# Revit family: Холодильные столы среднетемпературные
name_source: partatom
category: Оборудование
units: mm (PartAtom-declared; Revit-internal decimal feet)

## family parameters
Всегда вертикально = Да
Классификация = Нет
На основе рабочей плоскости = Нет
Общий = Нет
При загрузке вырезать с полостями = Нет
Размер круглого соединителя = Использовать диаметр
Тип детали = Нормальный
Точка расчета площади = Нет

## types (32) — shared parameters
Высота = 850 мм
Диап. рабочих темп. = -2....+10
Напряжение питания = 230.00 В
Степень защиты = IP24
Таблица поиска = ТМ
Температура окр. среды = +12.....-43
Терморегулятор = эл. блок
Тип оттайки = авт. с системой исп. конденсата
Тип охлаждения = динамический
Условия окр. среды (темп/влажн) = до +43/до 80
Хладаген = R134a
Холодильный стол = нержавеющая сталь
zero-valued in all types: Отметка по умолчанию

## per-type parameters (varying)
- ТМ2-GC: Боковая панель упр.=Да; Вес нетто/брутто, кг=125/140; Габаритные размеры, мм=1200х604х850/910; Глубина=604 мм; Двери 012-GC=Нет; Дверь G - 1=Нет; Дверь G-2=Нет; Дверь G-3=Нет; Дверь G-4=Нет; Дверь GC=Да; Количество дверей=2; Нижнее распол Дверь -1=Нет; Нижнее распол. Дверь -2=Нет; Нижняя панель упр.=Нет; Объем, л=270; Размеры в упоковке, мм=1310х715х1045; Столешница закругл.=Нет; Столешница квадр.=Да; Цена, руб=53 646; Число дверей=2; Ширина=1200 мм; Шкаф выдв. двойной - 1=Нет; Шкаф выдв. тройной - 1=Нет; Шкаф выдв. тройной - 2=Нет; Шкаф выдв.двойной - 2=Нет
- ТМ3-GC: Боковая панель упр.=Да; Вес нетто/брутто, кг=145/170; Габаритные размеры, мм=1630х605х850/910; Глубина=605 мм; Двери 012-GC=Нет; Дверь G - 1=Нет; Дверь G-2=Нет; Дверь G-3=Нет; Дверь G-4=Нет; Дверь GC=Да; Количество дверей=3; Нижнее распол Дверь -1=Нет; Нижнее распол. Дверь -2=Нет; Нижняя панель упр.=Нет; Объем, л=400; Размеры в упоковке, мм=1725х715х1045; Столешница закругл.=Нет; Столешница квадр.=Да; Цена, руб=63 011; Число дверей=3; Ширина=1630 мм; Шкаф выдв. двойной - 1=Нет; Шкаф выдв. тройной - 1=Нет; Шкаф выдв. тройной - 2=Нет; Шкаф выдв.двойной - 2=Нет
- TM4-GC: Боковая панель упр.=Да; Вес нетто/брутто, кг=165/190; Габаритные размеры, мм=2060х605х850/910; Глубина=605 мм; Двери 012-GC=Нет; Дверь G - 1=Нет; Дверь G-2=Нет; Дверь G-3=Нет; Дверь G-4=Нет; Дверь GC=Да; Количество дверей=4; Нижнее распол Дверь -1=Нет; Нижнее распол. Дверь -2=Нет; Нижняя панель упр.=Нет; Объем, л=500; Размеры в упоковке, мм=2165х715х1045; Столешница закругл.=Нет; Столешница квадр.=Да; Цена, руб=77 746; Число дверей=4; Ширина=2060 мм; Шкаф выдв. двойной - 1=Нет; Шкаф выдв. тройной - 1=Нет; Шкаф выдв. тройной - 2=Нет; Шкаф выдв.двойной - 2=Нет
- TM2GN-GC: Боковая панель упр.=Да; Вес нетто/брутто, кг=130/150; Габаритные размеры, мм=1200х605х850/910; Глубина=705 мм; Двери 012-GC=Нет; Дверь G - 1=Нет; Дверь G-2=Нет; Дверь G-3=Нет; Дверь G-4=Нет; Дверь GC=Да; Количество дверей=2; Нижнее распол Дверь -1=Нет; Нижнее распол. Дверь -2=Нет; Нижняя панель упр.=Нет; Объем, л=320; Размеры в упоковке, мм=1310х815х1045; Столешница закругл.=Нет; Столешница квадр.=Да; Цена, руб=55 169; Число дверей=2; Ширина=1200 мм; Шкаф выдв. двойной - 1=Нет; Шкаф выдв. тройной - 1=Нет; Шкаф выдв. тройной - 2=Нет; Шкаф выдв.двойной - 2=Нет
- TM3GN-GC: Боковая панель упр.=Да; Вес нетто/брутто, кг=150/180; Габаритные размеры, мм=1630х605х850/910; Глубина=705 мм; Двери 012-GC=Нет; Дверь G - 1=Нет; Дверь G-2=Нет; Дверь G-3=Нет; Дверь G-4=Нет; Дверь GC=Да; Количество дверей=3; Нижнее распол Дверь -1=Нет; Нижнее распол. Дверь -2=Нет; Нижняя панель упр.=Нет; Объем, л=450; Размеры в упоковке, мм=1725х815х1045; Столешница закругл.=Нет; Столешница квадр.=Да; Цена, руб=64 254; Число дверей=3; Ширина=1630 мм; Шкаф выдв. двойной - 1=Нет; Шкаф выдв. тройной - 1=Нет; Шкаф выдв. тройной - 2=Нет; Шкаф выдв.двойной - 2=Нет
- TM4GN-GC: Боковая панель упр.=Да; Вес нетто/брутто, кг=165/200; Габаритные размеры, мм=2060х605х850/910; Глубина=705 мм; Двери 012-GC=Нет; Дверь G - 1=Нет; Дверь G-2=Нет; Дверь G-3=Нет; Дверь G-4=Нет; Дверь GC=Да; Количество дверей=4; Нижнее распол Дверь -1=Нет; Нижнее распол. Дверь -2=Нет; Нижняя панель упр.=Нет; Объем, л=600; Размеры в упоковке, мм=2165х815х1045; Столешница закругл.=Нет; Столешница квадр.=Да; Цена, руб=78 641; Число дверей=4; Ширина=2060 мм; Шкаф выдв. двойной - 1=Нет; Шкаф выдв. тройной - 1=Нет; Шкаф выдв. тройной - 2=Нет; Шкаф выдв.двойной - 2=Нет
- TM2-G: Боковая панель упр.=Да; Вес нетто/брутто, кг=125/140; Габаритные размеры, мм=1200х604х850/910; Глубина=604 мм; Двери 012-GC=Нет; Дверь G - 1=Да; Дверь G-2=Да; Дверь G-3=Нет; Дверь G-4=Нет; Дверь GC=Нет; Количество дверей=2; Нижнее распол Дверь -1=Нет; Нижнее распол. Дверь -2=Нет; Нижняя панель упр.=Нет; Объем, л=270; Размеры в упоковке, мм=1310х715х1045; Столешница закругл.=Да; Столешница квадр.=Нет; Цена, руб=55 418; Число дверей=2; Ширина=1200 мм; Шкаф выдв. двойной - 1=Нет; Шкаф выдв. тройной - 1=Нет; Шкаф выдв. тройной - 2=Нет; Шкаф выдв.двойной - 2=Нет
- TM-4G: Боковая панель упр.=Да; Вес нетто/брутто, кг=160/190; Габаритные размеры, мм=2060х605х850/910; Глубина=605 мм; Двери 012-GC=Нет; Дверь G - 1=Да; Дверь G-2=Да; Дверь G-3=Да; Дверь G-4=Да; Дверь GC=Нет; Количество дверей=4; Нижнее распол Дверь -1=Нет; Нижнее распол. Дверь -2=Нет; Нижняя панель упр.=Нет; Объем, л=500; Размеры в упоковке, мм=2165х715х1045; Столешница закругл.=Да; Столешница квадр.=Нет; Цена, руб=78 828; Число дверей=2; Ширина=2060 мм; Шкаф выдв. двойной - 1=Нет; Шкаф выдв. тройной - 1=Нет; Шкаф выдв. тройной - 2=Нет; Шкаф выдв.двойной - 2=Нет
- ТМ3-G: Боковая панель упр.=Да; Вес нетто/брутто, кг=145/170; Габаритные размеры, мм=1630х605х850/910; Глубина=605 мм; Двери 012-GC=Нет; Дверь G - 1=Да; Дверь G-2=Да; Дверь G-3=Нет; Дверь G-4=Да; Дверь GC=Нет; Количество дверей=3; Нижнее распол Дверь -1=Нет; Нижнее распол. Дверь -2=Нет; Нижняя панель упр.=Нет; Объем, л=400; Размеры в упоковке, мм=1725х715х1045; Столешница закругл.=Да; Столешница квадр.=Нет; Цена, руб=65 047; Число дверей=2; Ширина=1630 мм; Шкаф выдв. двойной - 1=Нет; Шкаф выдв. тройной - 1=Нет; Шкаф выдв. тройной - 2=Нет; Шкаф выдв.двойной - 2=Нет
- TM2-22-G: Боковая панель упр.=Да; Вес нетто/брутто, кг=135/150; Габаритные размеры, мм=1200х605х850/910; Глубина=605 мм; Двери 012-GC=Нет; Дверь G - 1=Нет; Дверь G-2=Нет; Дверь G-3=Нет; Дверь G-4=Нет; Дверь GC=Нет; Количество дверей=2; Нижнее распол Дверь -1=Нет; Нижнее распол. Дверь -2=Нет; Нижняя панель упр.=Нет; Объем, л=270; Размеры в упоковке, мм=1310х715х1045; Столешница закругл.=Да; Столешница квадр.=Нет; Цена, руб=88 198; Число дверей=2; Ширина=1200 мм; Шкаф выдв. двойной - 1=Да; Шкаф выдв. тройной - 1=Нет; Шкаф выдв. тройной - 2=Нет; Шкаф выдв.двойной - 2=Да
- TM3-222-G: Боковая панель упр.=Да; Вес нетто/брутто, кг=160/185; Габаритные размеры, мм=1630х605х850/910; Глубина=605 мм; Двери 012-GC=Нет; Дверь G - 1=Нет; Дверь G-2=Нет; Дверь G-3=Нет; Дверь G-4=Нет; Дверь GC=Нет; Количество дверей=6; Нижнее распол Дверь -1=Нет; Нижнее распол. Дверь -2=Нет; Нижняя панель упр.=Нет; Объем, л=400; Размеры в упоковке, мм=1725х715х1045; Столешница закругл.=Да; Столешница квадр.=Нет; Цена, руб=114 216; Число дверей=2; Ширина=1630 мм; Шкаф выдв. двойной - 1=Да; Шкаф выдв. тройной - 1=Нет; Шкаф выдв. тройной - 2=Нет; Шкаф выдв.двойной - 2=Да
- TM3GN-222-G: Боковая панель упр.=Да; Вес нетто/брутто, кг=165/195; Габаритные размеры, мм=1630х705х850/910; Глубина=705 мм; Двери 012-GC=Нет; Дверь G - 1=Нет; Дверь G-2=Нет; Дверь G-3=Нет; Дверь G-4=Нет; Дверь GC=Нет; Количество дверей=6; Нижнее распол Дверь -1=Нет; Нижнее распол. Дверь -2=Нет; Нижняя панель упр.=Нет; Объем, л=450; Размеры в упоковке, мм=1725х815х1045; Столешница закругл.=Да; Столешница квадр.=Нет; Цена, руб=116 511; Число дверей=2; Ширина=1630 мм; Шкаф выдв. двойной - 1=Да; Шкаф выдв. тройной - 1=Нет; Шкаф выдв. тройной - 2=Нет; Шкаф выдв.двойной - 2=Да
- TM2GN-22-G: Боковая панель упр.=Да; Вес нетто/брутто, кг=140/160; Габаритные размеры, мм=1200х705х850/910; Глубина=705 мм; Двери 012-GC=Нет; Дверь G - 1=Нет; Дверь G-2=Нет; Дверь G-3=Нет; Дверь G-4=Нет; Дверь GC=Нет; Количество дверей=4; Нижнее распол Дверь -1=Нет; Нижнее распол. Дверь -2=Нет; Нижняя панель упр.=Нет; Объем, л=320; Размеры в упоковке, мм=1310х815х1045; Столешница закругл.=Да; Столешница квадр.=Нет; Цена, руб=89 679; Число дверей=2; Ширина=1200 мм; Шкаф выдв. двойной - 1=Да; Шкаф выдв. тройной - 1=Нет; Шкаф выдв. тройной - 2=Нет; Шкаф выдв.двойной - 2=Да
- TM2-20-G: Боковая панель упр.=Да; Вес нетто/брутто, кг=130/145; Габаритные размеры, мм=1200х605х850/910; Глубина=605 мм; Двери 012-GC=Нет; Дверь G - 1=Нет; Дверь G-2=Да; Дверь G-3=Нет; Дверь G-4=Нет; Дверь GC=Нет; Количество дверей=2; Нижнее распол Дверь -1=Нет; Нижнее распол. Дверь -2=Нет; Нижняя панель упр.=Нет; Объем, л=270; Размеры в упоковке, мм=1310х715х1045; Столешница закругл.=Да; Столешница квадр.=Нет; Цена, руб=71 808; Число дверей=2; Ширина=1200 мм; Шкаф выдв. двойной - 1=Да; Шкаф выдв. тройной - 1=Нет; Шкаф выдв. тройной - 2=Нет; Шкаф выдв.двойной - 2=Нет
- TM2GN-20-G: Боковая панель упр.=Да; Вес нетто/брутто, кг=135/155; Габаритные размеры, мм=1200х705х850/910; Глубина=705 мм; Двери 012-GC=Нет; Дверь G - 1=Нет; Дверь G-2=Да; Дверь G-3=Нет; Дверь G-4=Нет; Дверь GC=Нет; Количество дверей=2; Нижнее распол Дверь -1=Нет; Нижнее распол. Дверь -2=Нет; Нижняя панель упр.=Нет; Объем, л=320; Размеры в упоковке, мм=1310х815х1045; Столешница закругл.=Да; Столешница квадр.=Нет; Цена, руб=73 289; Число дверей=2; Ширина=1200 мм; Шкаф выдв. двойной - 1=Да; Шкаф выдв. тройной - 1=Нет; Шкаф выдв. тройной - 2=Нет; Шкаф выдв.двойной - 2=Нет
- TM2-33-G: Боковая панель упр.=Да; Вес нетто/брутто, кг=135/150; Габаритные размеры, мм=1200х605х850/910; Глубина=605 мм; Двери 012-GC=Нет; Дверь G - 1=Нет; Дверь G-2=Нет; Дверь G-3=Нет; Дверь G-4=Нет; Дверь GC=Нет; Количество дверей=2; Нижнее распол Дверь -1=Нет; Нижнее распол. Дверь -2=Нет; Нижняя панель упр.=Нет; Объем, л=270; Размеры в упоковке, мм=1310х715х1045; Столешница закругл.=Да; Столешница квадр.=Нет; Цена, руб=93 198; Число дверей=2; Ширина=1200 мм; Шкаф выдв. двойной - 1=Нет; Шкаф выдв. тройной - 1=Да; Шкаф выдв. тройной - 2=Да; Шкаф выдв.двойной - 2=Нет
- TM3-333-G: Боковая панель упр.=Да; Вес нетто/брутто, кг=160/185; Габаритные размеры, мм=1630х605х850/910; Глубина=605 мм; Двери 012-GC=Нет; Дверь G - 1=Нет; Дверь G-2=Нет; Дверь G-3=Нет; Дверь G-4=Нет; Дверь GC=Нет; Количество дверей=9; Нижнее распол Дверь -1=Нет; Нижнее распол. Дверь -2=Нет; Нижняя панель упр.=Нет; Объем, л=400; Размеры в упоковке, мм=1725х715х1045; Столешница закругл.=Да; Столешница квадр.=Нет; Цена, руб=121 716; Число дверей=2; Ширина=1630 мм; Шкаф выдв. двойной - 1=Нет; Шкаф выдв. тройной - 1=Да; Шкаф выдв. тройной - 2=Да; Шкаф выдв.двойной - 2=Нет
- TM2-03-G: Боковая панель упр.=Да; Вес нетто/брутто, кг=135/150; Габаритные размеры, мм=1200х605х850/910; Глубина=605 мм; Двери 012-GC=Нет; Дверь G - 1=Нет; Дверь G-2=Да; Дверь G-3=Нет; Дверь G-4=Нет; Дверь GC=Нет; Количество дверей=2; Нижнее распол Дверь -1=Нет; Нижнее распол. Дверь -2=Нет; Нижняя панель упр.=Нет; Объем, л=270; Размеры в упоковке, мм=1310х715х1045; Столешница закругл.=Да; Столешница квадр.=Нет; Цена, руб=74 308; Число дверей=2; Ширина=1200 мм; Шкаф выдв. двойной - 1=Нет; Шкаф выдв. тройной - 1=Да; Шкаф выдв. тройной - 2=Нет; Шкаф выдв.двойной - 2=Нет
- TM2GN-03-G: Боковая панель упр.=Да; Вес нетто/брутто, кг=135/155; Габаритные размеры, мм=1200х705х850/910; Глубина=705 мм; Двери 012-GC=Нет; Дверь G - 1=Нет; Дверь G-2=Да; Дверь G-3=Нет; Дверь G-4=Нет; Дверь GC=Нет; Количество дверей=2; Нижнее распол Дверь -1=Нет; Нижнее распол. Дверь -2=Нет; Нижняя панель упр.=Нет; Объем, л=270; Размеры в упоковке, мм=1310х815х1045; Столешница закругл.=Да; Столешница квадр.=Нет; Цена, руб=75 789; Число дверей=2; Ширина=1200 мм; Шкаф выдв. двойной - 1=Нет; Шкаф выдв. тройной - 1=Да; Шкаф выдв. тройной - 2=Нет; Шкаф выдв.двойной - 2=Нет
- TM3GN-333-G: Боковая панель упр.=Да; Вес нетто/брутто, кг=165/195; Габаритные размеры, мм=1630х705х850/910; Глубина=705 мм; Двери 012-GC=Нет; Дверь G - 1=Нет; Дверь G-2=Нет; Дверь G-3=Нет; Дверь G-4=Нет; Дверь GC=Нет; Количество дверей=9; Нижнее распол Дверь -1=Нет; Нижнее распол. Дверь -2=Нет; Нижняя панель упр.=Нет; Объем, л=450; Размеры в упоковке, мм=1725х815х1045; Столешница закругл.=Да; Столешница квадр.=Нет; Цена, руб=124 011; Число дверей=2; Ширина=1630 мм; Шкаф выдв. двойной - 1=Нет; Шкаф выдв. тройной - 1=Да; Шкаф выдв. тройной - 2=Да; Шкаф выдв.двойной - 2=Нет
- TM2GN-33-G: Боковая панель упр.=Да; Вес нетто/брутто, кг=140/160; Габаритные размеры, мм=1200х705х850/910; Глубина=705 мм; Двери 012-GC=Нет; Дверь G - 1=Нет; Дверь G-2=Нет; Дверь G-3=Нет; Дверь G-4=Нет; Дверь GC=Нет; Количество дверей=2; Нижнее распол Дверь -1=Нет; Нижнее распол. Дверь -2=Нет; Нижняя панель упр.=Нет; Объем, л=320; Размеры в упоковке, мм=1310х815х1045; Столешница закругл.=Да; Столешница квадр.=Нет; Цена, руб=94 679; Число дверей=2; Ширина=1200 мм; Шкаф выдв. двойной - 1=Нет; Шкаф выдв. тройной - 1=Да; Шкаф выдв. тройной - 2=Да; Шкаф выдв.двойной - 2=Нет
- TM3GN-012-GC: Боковая панель упр.=Да; Вес нетто/брутто, кг=160/190; Габаритные размеры, мм=1630х705х850/910; Глубина=705 мм; Двери 012-GC=Да; Дверь G - 1=Нет; Дверь G-2=Нет; Дверь G-3=Нет; Дверь G-4=Нет; Дверь GC=Нет; Количество дверей=5; Нижнее распол Дверь -1=Нет; Нижнее распол. Дверь -2=Нет; Нижняя панель упр.=Нет; Объем, л=450; Размеры в упоковке, мм=1725х815х1045; Столешница закругл.=Нет; Столешница квадр.=Да; Число дверей=3; Ширина=1630 мм; Шкаф выдв. двойной - 1=Нет; Шкаф выдв. тройной - 1=Нет; Шкаф выдв. тройной - 2=Нет; Шкаф выдв.двойной - 2=Нет
- TM3-012-GC: Боковая панель упр.=Да; Вес нетто/брутто, кг=140/180; Габаритные размеры, мм=1630х605х850/910; Глубина=605 мм; Двери 012-GC=Да; Дверь G - 1=Нет; Дверь G-2=Нет; Дверь G-3=Нет; Дверь G-4=Нет; Дверь GC=Нет; Количество дверей=5; Нижнее распол Дверь -1=Нет; Нижнее распол. Дверь -2=Нет; Нижняя панель упр.=Нет; Объем, л=400; Размеры в упоковке, мм=1725х715х1045; Столешница закругл.=Нет; Столешница квадр.=Да; Число дверей=3; Ширина=1630 мм; Шкаф выдв. двойной - 1=Нет; Шкаф выдв. тройной - 1=Нет; Шкаф выдв. тройной - 2=Нет; Шкаф выдв.двойной - 2=Нет
- TMi4-G: Боковая панель упр.=Нет; Вес нетто/брутто, кг=-; Габаритные размеры, мм=1850х600х850/910; Глубина=600 мм; Двери 012-GC=Нет; Дверь G - 1=Нет; Дверь G-2=Нет; Дверь G-3=Нет; Дверь G-4=Нет; Дверь GC=Нет; Количество дверей=4; Нижнее распол Дверь -1=Да; Нижнее распол. Дверь -2=Да; Нижняя панель упр.=Да; Объем, л=306; Размеры в упоковке, мм=2000х714х1040; Столешница закругл.=Да; Столешница квадр.=Нет; Цена, руб=79 990; Число дверей=2; Ширина=1850 мм; Шкаф выдв. двойной - 1=Нет; Шкаф выдв. тройной - 1=Нет; Шкаф выдв. тройной - 2=Нет; Шкаф выдв.двойной - 2=Нет
- TMi-2G: Боковая панель упр.=Нет; Вес нетто/брутто, кг=-; Габаритные размеры, мм=900х600х850/910; Глубина=600 мм; Двери 012-GC=Нет; Дверь G - 1=Нет; Дверь G-2=Нет; Дверь G-3=Нет; Дверь G-4=Нет; Дверь GC=Нет; Количество дверей=2; Нижнее распол Дверь -1=Да; Нижнее распол. Дверь -2=Нет; Нижняя панель упр.=Да; Объем, л=153; Размеры в упоковке, мм=1045х714х1040; Столешница закругл.=Да; Столешница квадр.=Нет; Цена, руб=39 741; Число дверей=2; Ширина=900 мм; Шкаф выдв. двойной - 1=Нет; Шкаф выдв. тройной - 1=Нет; Шкаф выдв. тройной - 2=Нет; Шкаф выдв.двойной - 2=Нет
- TMi-3G: Боковая панель упр.=Нет; Вес нетто/брутто, кг=-; Габаритные размеры, мм=1375х600х850/910; Глубина=600 мм; Двери 012-GC=Нет; Дверь G - 1=Нет; Дверь G-2=Нет; Дверь G-3=Нет; Дверь G-4=Нет; Дверь GC=Нет; Количество дверей=3; Нижнее распол Дверь -1=Да; Нижнее распол. Дверь -2=Нет; Нижняя панель упр.=Да; Объем, л=230; Размеры в упоковке, мм=1520х714х1040; Столешница закругл.=Да; Столешница квадр.=Нет; Цена, руб=64 100; Число дверей=2; Ширина=1375 мм; Шкаф выдв. двойной - 1=Нет; Шкаф выдв. тройной - 1=Нет; Шкаф выдв. тройной - 2=Нет; Шкаф выдв.двойной - 2=Нет
- TMi2GN-G: Боковая панель упр.=Нет; Вес нетто/брутто, кг=-; Габаритные размеры, мм=900х700х850/910; Глубина=700 мм; Двери 012-GC=Нет; Дверь G - 1=Нет; Дверь G-2=Нет; Дверь G-3=Нет; Дверь G-4=Нет; Дверь GC=Нет; Количество дверей=2; Нижнее распол Дверь -1=Да; Нижнее распол. Дверь -2=Нет; Нижняя панель упр.=Да; Объем, л=184; Размеры в упоковке, мм=1045х814х1040; Столешница закругл.=Да; Столешница квадр.=Нет; Цена, руб=49 940; Число дверей=2; Ширина=900 мм; Шкаф выдв. двойной - 1=Нет; Шкаф выдв. тройной - 1=Нет; Шкаф выдв. тройной - 2=Нет; Шкаф выдв.двойной - 2=Нет
- TMi3GN-G: Боковая панель упр.=Нет; Вес нетто/брутто, кг=-; Габаритные размеры, мм=1375х700х850/910; Глубина=700 мм; Двери 012-GC=Нет; Дверь G - 1=Нет; Дверь G-2=Нет; Дверь G-3=Нет; Дверь G-4=Нет; Дверь GC=Нет; Количество дверей=3; Нижнее распол Дверь -1=Да; Нижнее распол. Дверь -2=Нет; Нижняя панель упр.=Да; Объем, л=279; Размеры в упоковке, мм=1520х814х1040; Столешница закругл.=Да; Столешница квадр.=Нет; Цена, руб=67 400; Число дверей=2; Ширина=1375 мм; Шкаф выдв. двойной - 1=Нет; Шкаф выдв. тройной - 1=Нет; Шкаф выдв. тройной - 2=Нет; Шкаф выдв.двойной - 2=Нет
- TMi4GN-G: Боковая панель упр.=Нет; Вес нетто/брутто, кг=-; Габаритные размеры, мм=1850х700х850/910; Глубина=700 мм; Двери 012-GC=Нет; Дверь G - 1=Нет; Дверь G-2=Нет; Дверь G-3=Нет; Дверь G-4=Нет; Дверь GC=Нет; Количество дверей=4; Нижнее распол Дверь -1=Да; Нижнее распол. Дверь -2=Да; Нижняя панель упр.=Да; Объем, л=368; Размеры в упоковке, мм=2000х714х1040; Столешница закругл.=Да; Столешница квадр.=Нет; Цена, руб=84 400; Число дверей=2; Ширина=1850 мм; Шкаф выдв. двойной - 1=Нет; Шкаф выдв. тройной - 1=Нет; Шкаф выдв. тройной - 2=Нет; Шкаф выдв.двойной - 2=Нет
- TM2GN-G: Боковая панель упр.=Да; Вес нетто/брутто, кг=130/150; Габаритные размеры, мм=1200х705х850/910; Глубина=705 мм; Двери 012-GC=Нет; Дверь G - 1=Да; Дверь G-2=Да; Дверь G-3=Нет; Дверь G-4=Нет; Дверь GC=Нет; Количество дверей=2; Нижнее распол Дверь -1=Нет; Нижнее распол. Дверь -2=Нет; Нижняя панель упр.=Нет; Объем, л=320; Размеры в упоковке, мм=1310х815х1045; Столешница закругл.=Да; Столешница квадр.=Нет; Цена, руб=56 899; Число дверей=2; Ширина=1200 мм; Шкаф выдв. двойной - 1=Нет; Шкаф выдв. тройной - 1=Нет; Шкаф выдв. тройной - 2=Нет; Шкаф выдв.двойной - 2=Нет
- TM3GN-G: Боковая панель упр.=Да; Вес нетто/брутто, кг=150/180; Габаритные размеры, мм=1630х705х850/910; Глубина=705 мм; Двери 012-GC=Нет; Дверь G - 1=Да; Дверь G-2=Да; Дверь G-3=Нет; Дверь G-4=Да; Дверь GC=Нет; Количество дверей=3; Нижнее распол Дверь -1=Нет; Нижнее распол. Дверь -2=Нет; Нижняя панель упр.=Нет; Объем, л=450; Размеры в упоковке, мм=1725х815х1045; Столешница закругл.=Да; Столешница квадр.=Нет; Цена, руб=67 342; Число дверей=2; Ширина=1630 мм; Шкаф выдв. двойной - 1=Нет; Шкаф выдв. тройной - 1=Нет; Шкаф выдв. тройной - 2=Нет; Шкаф выдв.двойной - 2=Нет
- TM4GN-G: Боковая панель упр.=Да; Вес нетто/брутто, кг=160/200; Габаритные размеры, мм=2060х705х850/910; Глубина=705 мм; Двери 012-GC=Нет; Дверь G - 1=Да; Дверь G-2=Да; Дверь G-3=Да; Дверь G-4=Да; Дверь GC=Нет; Количество дверей=4; Нижнее распол Дверь -1=Нет; Нижнее распол. Дверь -2=Нет; Нижняя панель упр.=Нет; Объем, л=600; Размеры в упоковке, мм=2165х815х1045; Столешница закругл.=Да; Столешница квадр.=Нет; Цена, руб=80 219; Число дверей=2; Ширина=2060 мм; Шкаф выдв. двойной - 1=Нет; Шкаф выдв. тройной - 1=Нет; Шкаф выдв. тройной - 2=Нет; Шкаф выдв.двойной - 2=Нет
